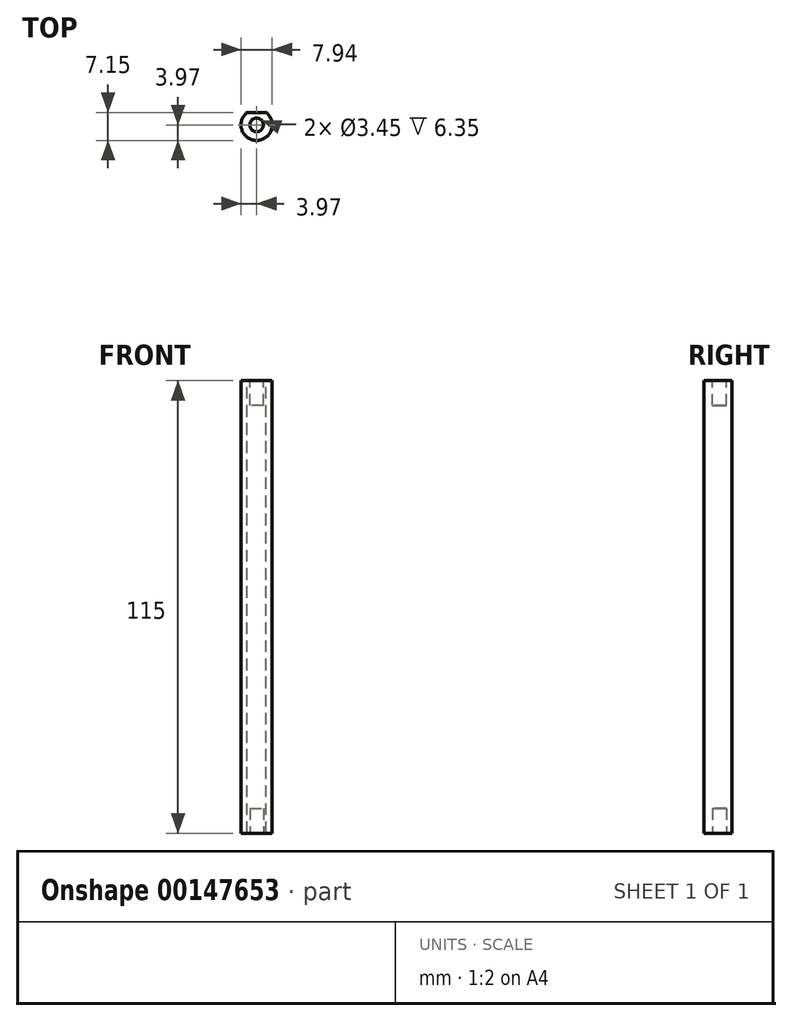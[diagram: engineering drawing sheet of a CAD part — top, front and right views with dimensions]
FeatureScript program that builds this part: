
annotation { "Feature Type Name" : "Feature", "Feature Type Description" : "" }
export const myFeature = defineFeature(function(context is Context, id is Id, definition is map)
    precondition{}
    {
        {
            var Q0;
            Q0=qCreatedBy(makeId("Top.planeOp"),FACE);
            var sketch = newSketch(context, id + "F0", { "sketchPlane" : qUnion([Q0])});
            skCircle(sketch, "E0", {"center": v(0, 0) * mm, "radius": 3.97 * mm});
            skSolve(sketch);
        }
        {
            var Q0;
            Q0=qSketchRegion(id+"F0",true);
            extrude(context, id + "F1", {"entities" : qUnion([Q0]), "depth" : 115 * mm});
        }
        {
            var Q0;
            Q0=makeQuery(id+"F1.opExtrude","CAP_FACE",FACE,{"disambiguationData":[OSD([sQuery(id+"F0.wireOp",EDGE,"E0")])],"isStart":false});
            var sketch = newSketch(context, id + "F2", { "sketchPlane" : qUnion([Q0])});
            skLineSegment(sketch, "E1.bottom", {"start": v(-2.38, 3.17) * mm, "end": v(2.38, 3.17) * mm});
            skLineSegment(sketch, "E1.top", {"start": v(-2.38, 3.97) * mm, "end": v(2.38, 3.97) * mm});
            skLineSegment(sketch, "E1.left", {"start": v(-2.38, 3.17) * mm, "end": v(-2.38, 3.97) * mm});
            skLineSegment(sketch, "E1.right", {"start": v(2.38, 3.17) * mm, "end": v(2.38, 3.97) * mm});
            skSolve(sketch);
        }
        {
            var Q0;
            Q0=qSketchRegion(id+"F2",true);
            var Q1;
            Q1=makeQuery(id+"F1.opExtrude","CAP_FACE",FACE,{"disambiguationData":[OSD([sQuery(id+"F0.wireOp",EDGE,"E0")])],"isStart":true});
            extrude(context, id + "F3", {"entities" : qUnion([Q0]), "operationType" : NewBodyOperationType.REMOVE, "endBound" : BoundingType.UP_TO_SURFACE, "oppositeDirection" : true, "endBoundEntityFace" : qUnion([Q1]), "depth" : 25.4 * mm});
        }
        {
            var Q0;
            Q0=makeQuery(id+"F1.opExtrude","CAP_FACE",FACE,{"disambiguationData":[OSD([sQuery(id+"F0.wireOp",EDGE,"E0")])],"isStart":true});
            var sketch = newSketch(context, id + "F4", { "sketchPlane" : qUnion([Q0])});
            skCircle(sketch, "E2", {"center": v(0, 0) * mm, "radius": 1.73 * mm});
            skSolve(sketch);
        }
        {
            var Q0;
            Q0=qSketchRegion(id+"F4",true);
            extrude(context, id + "F5", {"entities" : qUnion([Q0]), "operationType" : NewBodyOperationType.REMOVE, "oppositeDirection" : true, "depth" : 6.35 * mm});
        }
        {
            var Q0;
            Q0=makeQuery(id+"F1.opExtrude","CAP_FACE",FACE,{"disambiguationData":[OSD([sQuery(id+"F0.wireOp",EDGE,"E0")])],"isStart":false});
            var sketch = newSketch(context, id + "F6", { "sketchPlane" : qUnion([Q0])});
            skCircle(sketch, "E3", {"center": v(0, 0) * mm, "radius": 1.73 * mm});
            skSolve(sketch);
        }
        {
            var Q0;
            Q0=qSketchRegion(id+"F6",true);
            extrude(context, id + "F7", {"entities" : qUnion([Q0]), "operationType" : NewBodyOperationType.REMOVE, "oppositeDirection" : true, "depth" : 6.35 * mm});
        }
    });
